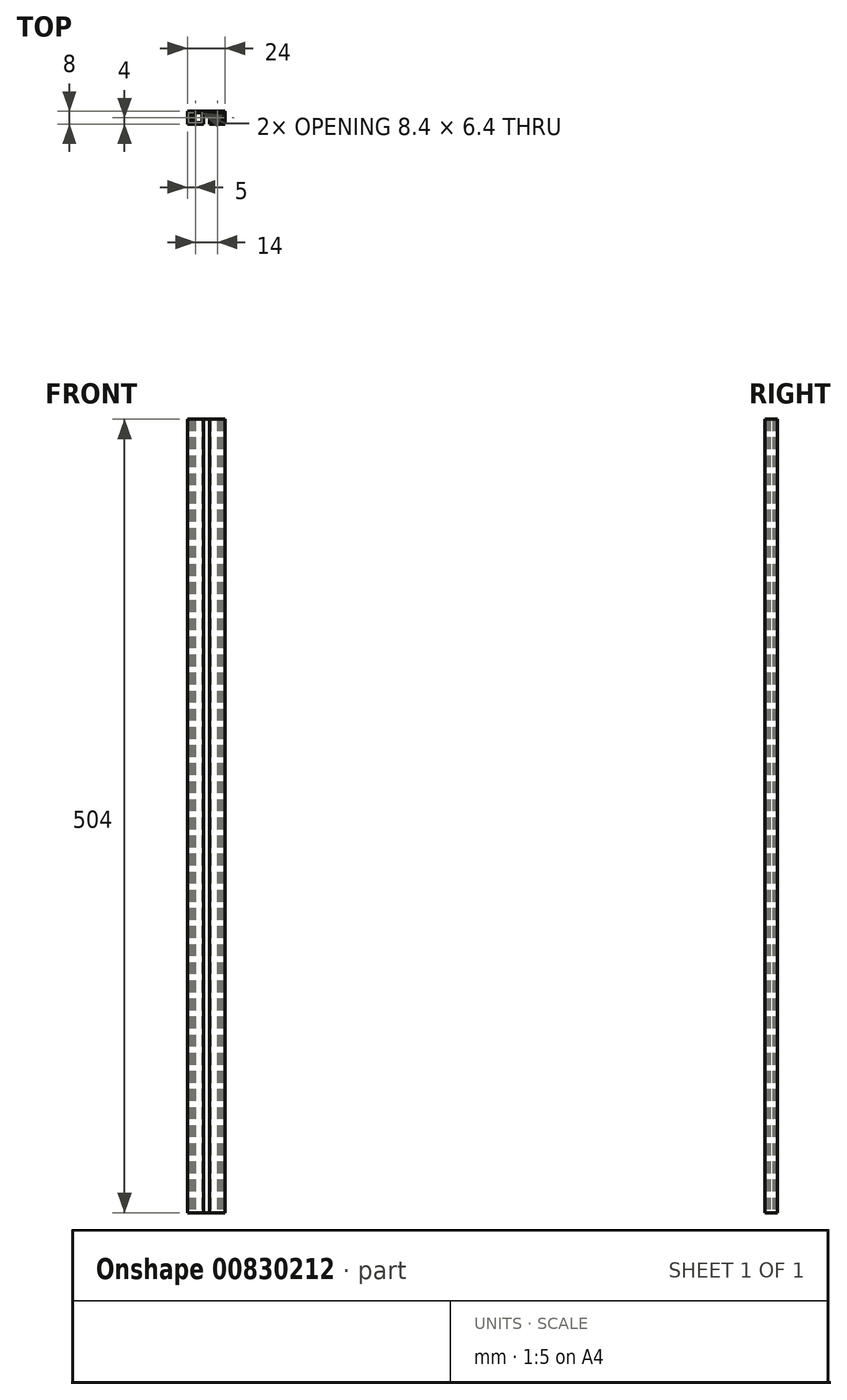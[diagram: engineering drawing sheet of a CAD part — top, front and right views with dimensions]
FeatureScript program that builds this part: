
annotation { "Feature Type Name" : "Feature", "Feature Type Description" : "" }
export const myFeature = defineFeature(function(context is Context, id is Id, definition is map)
    precondition{}
    {
        {
            var Q0;
            Q0=qCreatedBy(makeId("Top.planeOp"),FACE);
            var sketch = newSketch(context, id + "F0", { "sketchPlane" : qUnion([Q0])});
            skLineSegment(sketch, "E0.bottom", {"start": v(-12, 4) * mm, "end": v(12, 4) * mm});
            skLineSegment(sketch, "E0.top", {"start": v(-12, -4) * mm, "end": v(-1.9, -4) * mm});
            skLineSegment(sketch, "E0.left", {"start": v(-12, 4) * mm, "end": v(-12, -4) * mm});
            skLineSegment(sketch, "E0.right", {"start": v(12, 4) * mm, "end": v(12, -4) * mm});
            skLineSegment(sketch, "E1.top", {"start": v(-1.9, 2.8) * mm, "end": v(1.9, 2.8) * mm});
            skLineSegment(sketch, "E1.left", {"start": v(-1.9, -4) * mm, "end": v(-1.9, 2.8) * mm});
            skLineSegment(sketch, "E1.right", {"start": v(1.9, -4) * mm, "end": v(1.9, 2.8) * mm});
            skLineSegment(sketch, "E2.bottom", {"start": v(-11.2, -3.2) * mm, "end": v(-9.62, -3.2) * mm});
            skLineSegment(sketch, "E2.top", {"start": v(-7.95, 3.2) * mm, "end": v(-2.8, 3.2) * mm});
            skLineSegment(sketch, "E2.left", {"start": v(-11.2, -3.2) * mm, "end": v(-11.2, 3.2) * mm});
            skLineSegment(sketch, "E2.right", {"start": v(-2.8, -3.2) * mm, "end": v(-2.8, 3.2) * mm});
            skLineSegment(sketch, "E3.trimOffspring", {"start": v(1.9, -4) * mm, "end": v(12, -4) * mm});
            skLineSegment(sketch, "E4", {"start": v(-10.39, 1.22) * mm, "end": v(-10.39, 1.4) * mm});
            skLineSegment(sketch, "E5", {"start": v(-7.19, 1.22) * mm, "end": v(-7.19, 1.4) * mm});
            skArc(sketch, "E6", {"start": v(-7.19, 1.22) * mm, "mid": v(-7.32, 1.03) * mm, "end": v(-7.54, 1.08) * mm});
            skArc(sketch, "E7", {"start": v(-10.39, 1.22) * mm, "mid": v(-10.26, 1.03) * mm, "end": v(-10.04, 1.09) * mm});
            skArc(sketch, "E8", {"start": v(-10.39, 1.4) * mm, "mid": v(-10.31, 1.78) * mm, "end": v(-10.1, 2.1) * mm});
            skArc(sketch, "E9", {"start": v(-7.19, 1.4) * mm, "mid": v(-7.26, 1.78) * mm, "end": v(-7.48, 2.1) * mm});
            skLineSegment(sketch, "E10", {"start": v(-10.1, 2.1) * mm, "end": v(-9.5, 2.7) * mm});
            skLineSegment(sketch, "E11", {"start": v(-7.48, 2.1) * mm, "end": v(-8.08, 2.7) * mm});
            skArc(sketch, "E12", {"start": v(-8.08, 2.7) * mm, "mid": v(-8.15, 2.99) * mm, "end": v(-7.95, 3.2) * mm});
            skArc(sketch, "E13", {"start": v(-9.5, 2.7) * mm, "mid": v(-9.42, 2.99) * mm, "end": v(-9.62, 3.2) * mm});
            skPoint(sketch, "E14", {"position": v(-8.8, 0) * mm});
            skLineSegment(sketch, "E15", {"start": v(-11.2, 3.2) * mm, "end": v(-9.62, 3.2) * mm});
            skArc(sketch, "E16.trimOffspring", {"start": v(-7.54, 1.08) * mm, "mid": v(-8.79, 1.66) * mm, "end": v(-10.04, 1.09) * mm});
            skLineSegment(sketch, "E17.MirrorCS", {"start": v(-7.95, -3.2) * mm, "end": v(-2.8, -3.2) * mm});
            skLineSegment(sketch, "E18.MirrorCS", {"start": v(-7.19, -1.22) * mm, "end": v(-7.19, -1.4) * mm});
            skLineSegment(sketch, "E19.MirrorCS", {"start": v(-10.39, -1.22) * mm, "end": v(-10.39, -1.4) * mm});
            skArc(sketch, "E20.MirrorCS", {"start": v(-10.39, -1.22) * mm, "mid": v(-10.26, -1.03) * mm, "end": v(-10.04, -1.09) * mm});
            skArc(sketch, "E21.MirrorCS", {"start": v(-7.19, -1.22) * mm, "mid": v(-7.32, -1.03) * mm, "end": v(-7.54, -1.08) * mm});
            skLineSegment(sketch, "E22.MirrorCS", {"start": v(-7.48, -2.1) * mm, "end": v(-8.08, -2.7) * mm});
            skLineSegment(sketch, "E23.MirrorCS", {"start": v(-10.1, -2.1) * mm, "end": v(-9.5, -2.7) * mm});
            skArc(sketch, "E24.MirrorCS", {"start": v(-7.19, -1.4) * mm, "mid": v(-7.26, -1.78) * mm, "end": v(-7.48, -2.1) * mm});
            skArc(sketch, "E25.MirrorCS", {"start": v(-8.08, -2.7) * mm, "mid": v(-8.15, -2.99) * mm, "end": v(-7.95, -3.2) * mm});
            skArc(sketch, "E26.MirrorCS", {"start": v(-10.39, -1.4) * mm, "mid": v(-10.31, -1.78) * mm, "end": v(-10.1, -2.1) * mm});
            skArc(sketch, "E27.MirrorCS", {"start": v(-9.5, -2.7) * mm, "mid": v(-9.42, -2.99) * mm, "end": v(-9.62, -3.2) * mm});
            skArc(sketch, "E28.MirrorCS", {"start": v(-7.54, -1.08) * mm, "mid": v(-8.79, -1.66) * mm, "end": v(-10.04, -1.09) * mm});
            skLineSegment(sketch, "E29.MirrorCS", {"start": v(7.19, 1.22) * mm, "end": v(7.19, 1.4) * mm});
            skLineSegment(sketch, "E30.MirrorCS", {"start": v(7.48, 2.1) * mm, "end": v(8.08, 2.7) * mm});
            skArc(sketch, "E31.MirrorCS", {"start": v(10.39, -1.22) * mm, "mid": v(10.26, -1.03) * mm, "end": v(10.04, -1.09) * mm});
            skLineSegment(sketch, "E32.MirrorCS", {"start": v(10.39, -1.22) * mm, "end": v(10.39, -1.4) * mm});
            skArc(sketch, "E33.MirrorCS", {"start": v(7.19, 1.4) * mm, "mid": v(7.26, 1.78) * mm, "end": v(7.48, 2.1) * mm});
            skArc(sketch, "E34.MirrorCS", {"start": v(7.19, -1.22) * mm, "mid": v(7.32, -1.03) * mm, "end": v(7.54, -1.08) * mm});
            skArc(sketch, "E35.MirrorCS", {"start": v(9.5, -2.7) * mm, "mid": v(9.42, -2.99) * mm, "end": v(9.62, -3.2) * mm});
            skLineSegment(sketch, "E36.MirrorCS", {"start": v(7.48, -2.1) * mm, "end": v(8.08, -2.7) * mm});
            skArc(sketch, "E37.MirrorCS", {"start": v(7.19, -1.4) * mm, "mid": v(7.26, -1.78) * mm, "end": v(7.48, -2.1) * mm});
            skArc(sketch, "E38.MirrorCS", {"start": v(8.08, 2.7) * mm, "mid": v(8.15, 2.99) * mm, "end": v(7.95, 3.2) * mm});
            skArc(sketch, "E39.MirrorCS", {"start": v(9.5, 2.7) * mm, "mid": v(9.42, 2.99) * mm, "end": v(9.62, 3.2) * mm});
            skArc(sketch, "E40.MirrorCS", {"start": v(10.39, -1.4) * mm, "mid": v(10.31, -1.78) * mm, "end": v(10.1, -2.1) * mm});
            skLineSegment(sketch, "E41.MirrorCS", {"start": v(7.19, -1.22) * mm, "end": v(7.19, -1.4) * mm});
            skArc(sketch, "E42.MirrorCS", {"start": v(7.19, 1.22) * mm, "mid": v(7.32, 1.03) * mm, "end": v(7.54, 1.08) * mm});
            skLineSegment(sketch, "E43.MirrorCS", {"start": v(10.39, 1.22) * mm, "end": v(10.39, 1.4) * mm});
            skLineSegment(sketch, "E44.MirrorCS", {"start": v(10.1, 2.1) * mm, "end": v(9.5, 2.7) * mm});
            skArc(sketch, "E45.MirrorCS", {"start": v(10.39, 1.4) * mm, "mid": v(10.31, 1.78) * mm, "end": v(10.1, 2.1) * mm});
            skArc(sketch, "E46.MirrorCS", {"start": v(8.08, -2.7) * mm, "mid": v(8.15, -2.99) * mm, "end": v(7.95, -3.2) * mm});
            skArc(sketch, "E47.MirrorCS", {"start": v(10.39, 1.22) * mm, "mid": v(10.26, 1.03) * mm, "end": v(10.04, 1.09) * mm});
            skLineSegment(sketch, "E48.MirrorCS", {"start": v(10.1, -2.1) * mm, "end": v(9.5, -2.7) * mm});
            skArc(sketch, "E49.MirrorCS", {"start": v(7.54, 1.08) * mm, "mid": v(8.79, 1.66) * mm, "end": v(10.04, 1.09) * mm});
            skLineSegment(sketch, "E50.MirrorCS", {"start": v(11.2, -3.2) * mm, "end": v(9.62, -3.2) * mm});
            skLineSegment(sketch, "E51.MirrorCS", {"start": v(11.2, 3.2) * mm, "end": v(9.62, 3.2) * mm});
            skLineSegment(sketch, "E52.MirrorCS", {"start": v(7.95, -3.2) * mm, "end": v(2.8, -3.2) * mm});
            skLineSegment(sketch, "E53.MirrorCS", {"start": v(11.2, -3.2) * mm, "end": v(11.2, 3.2) * mm});
            skLineSegment(sketch, "E54.MirrorCS", {"start": v(2.8, -3.2) * mm, "end": v(2.8, 3.2) * mm});
            skLineSegment(sketch, "E55.MirrorCS", {"start": v(7.95, 3.2) * mm, "end": v(2.8, 3.2) * mm});
            skArc(sketch, "E56.MirrorCS", {"start": v(7.54, -1.08) * mm, "mid": v(8.79, -1.66) * mm, "end": v(10.04, -1.09) * mm});
            skPoint(sketch, "E57.MirrorP", {"position": v(8.8, 0) * mm});
            skSolve(sketch);
        }
        {
            var Q0;
            Q0 = qSketchRegion(id + "F0", true);
            extrude(context, id + "F1", {"entities" : qUnion([Q0]), "depth" : 504 * mm, "offsetDistance" : 25 * mm});
        }
    });
